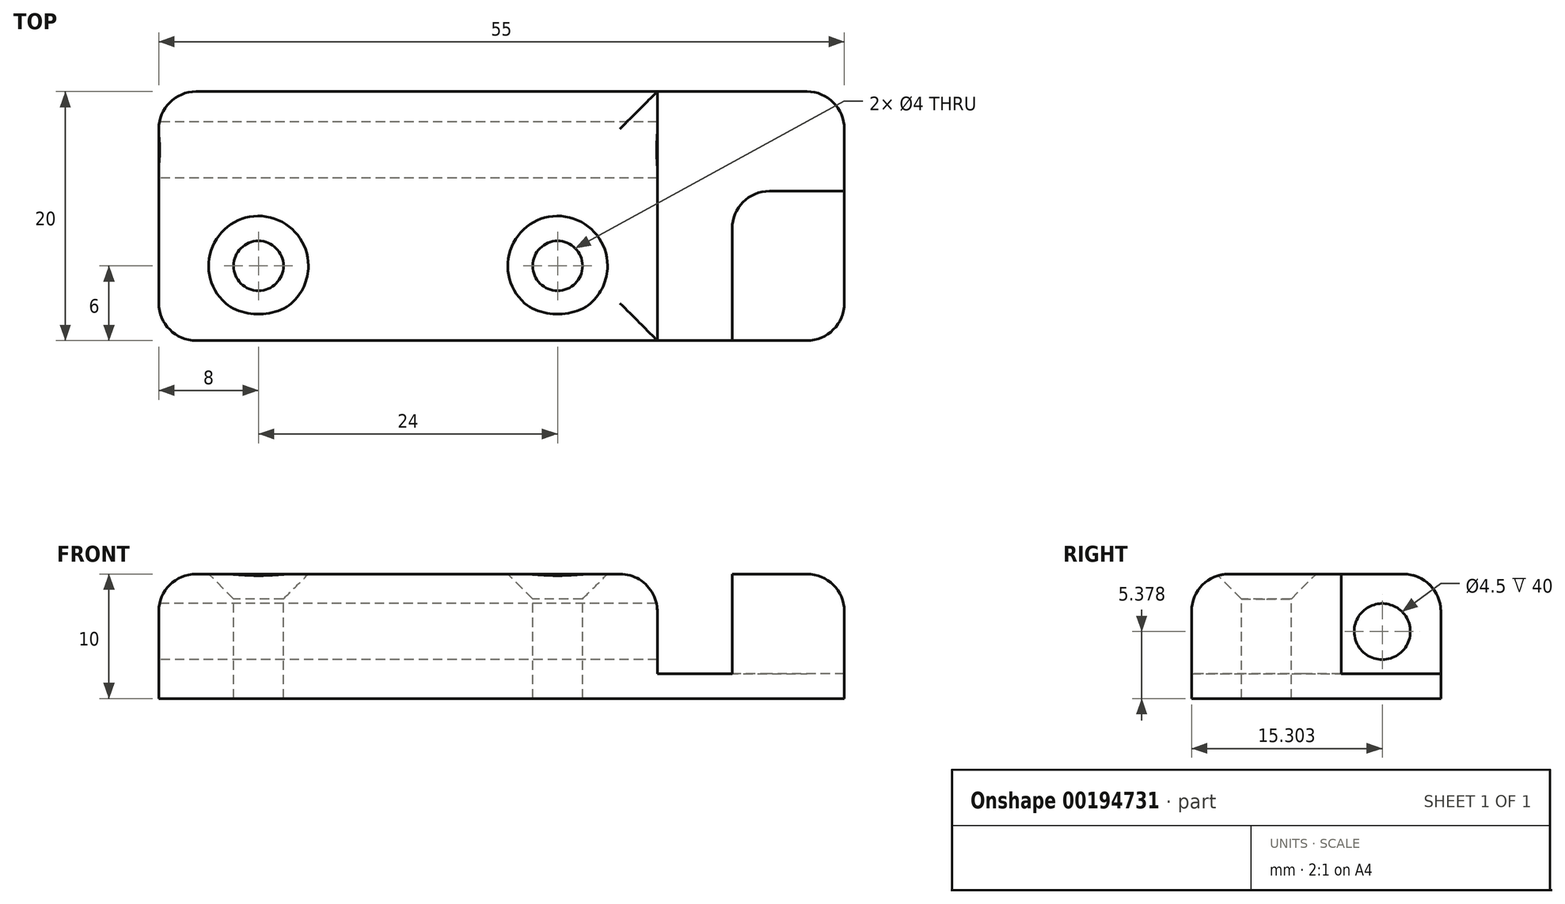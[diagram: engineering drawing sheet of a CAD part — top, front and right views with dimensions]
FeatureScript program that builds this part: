
annotation { "Feature Type Name" : "Feature", "Feature Type Description" : "" }
export const myFeature = defineFeature(function(context is Context, id is Id, definition is map)
    precondition{}
    {
        {
            var Q0;
            Q0=qCreatedBy(makeId("Top.planeOp"),FACE);
            var sketch = newSketch(context, id + "F0", { "sketchPlane" : qUnion([Q0])});
            skLineSegment(sketch, "E0.bottom", {"start": v(0, 0) * mm, "end": v(55, 0) * mm});
            skLineSegment(sketch, "E0.top", {"start": v(0, 20) * mm, "end": v(55, 20) * mm});
            skLineSegment(sketch, "E0.left", {"start": v(0, 0) * mm, "end": v(0, 20) * mm});
            skLineSegment(sketch, "E0.right", {"start": v(55, 0) * mm, "end": v(55, 20) * mm});
            skSolve(sketch);
        }
        {
            var Q0;
            Q0 = qSketchRegion(id + "F0", true);
            extrude(context, id + "F1", {"entities" : qUnion([Q0]), "depth" : 2 * mm});
        }
        {
            var Q0;
            Q0=makeQuery(id+"F1.opExtrude","CAP_FACE",FACE,{"disambiguationData":[OSD([sQuery(id+"F0.wireOp",EDGE,"E0.bottom"),sQuery(id+"F0.wireOp",EDGE,"E0.top"),sQuery(id+"F0.wireOp",EDGE,"E0.left"),sQuery(id+"F0.wireOp",EDGE,"E0.right")])],"isStart":false});
            var sketch = newSketch(context, id + "F2", { "sketchPlane" : qUnion([Q0])});
            skLineSegment(sketch, "E1.bottom", {"start": v(0, 0) * mm, "end": v(40, 0) * mm});
            skLineSegment(sketch, "E1.top", {"start": v(0, 20) * mm, "end": v(40, 20) * mm});
            skLineSegment(sketch, "E1.left", {"start": v(0, 0) * mm, "end": v(0, 20) * mm});
            skLineSegment(sketch, "E1.right", {"start": v(40, 0) * mm, "end": v(40, 20) * mm});
            skPoint(sketch, "E2.endSnap0", {"position": v(55, 10) * mm});
            skLineSegment(sketch, "E3.bottom", {"start": v(55, 12) * mm, "end": v(46, 12) * mm});
            skLineSegment(sketch, "E3.top", {"start": v(55, 0) * mm, "end": v(46, 0) * mm});
            skLineSegment(sketch, "E3.left", {"start": v(55, 12) * mm, "end": v(55, 0) * mm});
            skLineSegment(sketch, "E3.right", {"start": v(46, 12) * mm, "end": v(46, 0) * mm});
            skSolve(sketch);
        }
        {
            var Q0;
            Q0=makeQuery(id+"F2.imprint","IMPRINT",FACE,{"disambiguationData":[TD([[makeQuery(id+"F2.imprint","IMPRINT",EDGE,{"derivedFrom":sQuery(id+"F2.wireOp",EDGE,"E1.bottom")}),1.0]])]});
            var Q1;
            Q1=makeQuery(id+"F2.imprint","IMPRINT",FACE,{"disambiguationData":[TD([[makeQuery(id+"F2.imprint","IMPRINT",EDGE,{"derivedFrom":sQuery(id+"F2.wireOp",EDGE,"E3.bottom")}),1.0]])]});
            extrude(context, id + "F3", {"entities" : qUnion([Q0, Q1]), "operationType" : NewBodyOperationType.ADD, "depth" : 8 * mm});
        }
        {
            var Q0;
            Q0=makeQuery(id+"F3.boolean.opBoolean","MERGE",FACE,{"derivedFrom":[makeQuery(id+"F1.opExtrude","SWEPT_FACE",FACE,{"disambiguationData":[OSD([sQuery(id+"F0.wireOp",EDGE,"E0.left")])]}),makeQuery(id+"F3.opExtrude","SWEPT_FACE",FACE,{"disambiguationData":[OSD([sQuery(id+"F2.wireOp",EDGE,"E1.left")])]})]});
            var sketch = newSketch(context, id + "F4", { "sketchPlane" : qUnion([Q0])});
            skCircle(sketch, "E4", {"center": v(-15.3, 5.38) * mm, "radius": 2.25 * mm});
            skLineSegment(sketch, "E5", {"start": v(-14.14, 5.38) * mm, "end": v(-15.3, 5.38) * mm});
            skSolve(sketch);
        }
        {
            var Q0;
            Q0=makeQuery(id+"F4.imprint","IMPRINT",FACE,{"disambiguationData":[TD([[makeQuery(id+"F4.imprint","IMPRINT",EDGE,{"derivedFrom":sQuery(id+"F4.wireOp",EDGE,"E4")}),1.0]])]});
            extrude(context, id + "F5", {"entities" : qUnion([Q0]), "operationType" : NewBodyOperationType.REMOVE, "oppositeDirection" : true, "depth" : 45 * mm});
        }
        {
            var Q0;
            Q0=makeQuery(id+"F3.opExtrude","CAP_FACE",FACE,{"disambiguationData":[OSD([sQuery(id+"F2.wireOp",EDGE,"E1.bottom"),sQuery(id+"F2.wireOp",EDGE,"E1.top"),sQuery(id+"F2.wireOp",EDGE,"E1.left"),sQuery(id+"F2.wireOp",EDGE,"E1.right")])],"isStart":false});
            var sketch = newSketch(context, id + "F6", { "sketchPlane" : qUnion([Q0])});
            skCircle(sketch, "E6", {"center": v(8, 6) * mm, "radius": 2 * mm});
            skCircle(sketch, "E7", {"center": v(32, 6) * mm, "radius": 2 * mm});
            skCircle(sketch, "E8", {"center": v(8, 6) * mm, "radius": 4 * mm});
            skCircle(sketch, "E9", {"center": v(32, 6) * mm, "radius": 4 * mm});
            skSolve(sketch);
        }
        {
            var Q0;
            Q0=makeQuery(id+"F6.imprint","IMPRINT",FACE,{"disambiguationData":[TD([[makeQuery(id+"F6.imprint","IMPRINT",EDGE,{"derivedFrom":sQuery(id+"F6.wireOp",EDGE,"E6")}),1.0]])]});
            var Q1;
            Q1=makeQuery(id+"F6.imprint","IMPRINT",FACE,{"disambiguationData":[TD([[makeQuery(id+"F6.imprint","IMPRINT",EDGE,{"derivedFrom":sQuery(id+"F6.wireOp",EDGE,"E7")}),1.0]])]});
            extrude(context, id + "F7", {"entities" : qUnion([Q0, Q1]), "operationType" : NewBodyOperationType.REMOVE, "oppositeDirection" : true, "depth" : 25 * mm});
        }
        {
            var Q0;
            Q0=makeQuery(id+"F3.opExtrude","CAP_EDGE",EDGE,{"disambiguationData":[OSD([sQuery(id+"F2.wireOp",EDGE,"E1.top")])],"isStart":false});
            var Q1;
            Q1=makeQuery(id+"F3.opExtrude","CAP_EDGE",EDGE,{"disambiguationData":[OSD([sQuery(id+"F2.wireOp",EDGE,"E1.bottom")])],"isStart":false});
            var Q2;
            Q2=makeQuery(id+"F3.opExtrude","CAP_EDGE",EDGE,{"disambiguationData":[OSD([sQuery(id+"F2.wireOp",EDGE,"E3.top")])],"isStart":false});
            var Q3;
            Q3=makeQuery(id+"F3.opExtrude","CAP_EDGE",EDGE,{"disambiguationData":[OSD([sQuery(id+"F2.wireOp",EDGE,"E1.left")])],"isStart":false});
            var Q4;
            Q4=makeQuery(id+"F3.opExtrude","CAP_EDGE",EDGE,{"disambiguationData":[OSD([sQuery(id+"F2.wireOp",EDGE,"E1.right")])],"isStart":false});
            var Q5;
            Q5=makeQuery(id+"F1.opExtrude","SWEPT_EDGE",EDGE,{"disambiguationData":[OSD([sQuery(id+"F0.wireOp",EDGE,"E0.top"),sQuery(id+"F0.wireOp",EDGE,"E0.right")])]});
            fillet(context, id + "F8", {"entities" : qUnion([Q0, Q1, Q2, Q3, Q4, Q5]), "radius" : 3 * mm, "tangentPropagation" : true, "allowEdgeOverflow" : false});
        }
        {
            var Q0;
            Q0=makeQuery(id+"F3.opExtrude","CAP_FACE",FACE,{"disambiguationData":[OSD([sQuery(id+"F2.wireOp",EDGE,"E1.bottom"),sQuery(id+"F2.wireOp",EDGE,"E1.top"),sQuery(id+"F2.wireOp",EDGE,"E1.left"),sQuery(id+"F2.wireOp",EDGE,"E1.right")])],"isStart":false});
            var sketch = newSketch(context, id + "F9", { "sketchPlane" : qUnion([Q0])});
            skPoint(sketch, "E10", {"position": v(8, 6) * mm});
            skPoint(sketch, "E11", {"position": v(32, 6) * mm});
            skSolve(sketch);
        }
        {
            var Q0;
            Q0=sQuery(id+"F9.wireOp",VERTEX,"E10");
            var Q1;
            Q1=sQuery(id+"F9.wireOp",VERTEX,"E11");
            var Q2;
            Q2=makeQuery(id+"F1.opExtrude","SWEPT_BODY",BODY,{"disambiguationData":[OSD([sQuery(id+"F0.wireOp",EDGE,"E0.bottom"),sQuery(id+"F0.wireOp",EDGE,"E0.top"),sQuery(id+"F0.wireOp",EDGE,"E0.left"),sQuery(id+"F0.wireOp",EDGE,"E0.right")])]});
            hole(context, id + "F10", {"style" : HoleStyle.C_SINK, "endStyle" : HoleEndStyle.BLIND, "holeDiameter" : 4 * mm, "cSinkDiameter" : 8 * mm, "cSinkAngle" : 90 * degree, "holeDepth" : 20 * mm, "isTappedThrough" : true, "tappedDepth" : 12 * mm, "tapClearance" : 3, "startFromSketch" : true, "locations" : qUnion([Q0, Q1]), "scope" : qUnion([Q2])});
        }
        {
            var Q0;
            Q0=makeQuery(id+"F3.boolean.opBoolean","MERGE",EDGE,{"derivedFrom":[makeQuery(id+"F1.opExtrude","SWEPT_EDGE",EDGE,{"disambiguationData":[OSD([sQuery(id+"F0.wireOp",EDGE,"E0.bottom"),sQuery(id+"F0.wireOp",EDGE,"E0.left")])]}),makeQuery(id+"F3.opExtrude","SWEPT_EDGE",EDGE,{"disambiguationData":[OSD([sQuery(id+"F2.wireOp",EDGE,"E1.bottom"),sQuery(id+"F2.wireOp",EDGE,"E1.left")])]})]});
            var Q1;
            Q1=makeQuery(id+"F3.boolean.opBoolean","MERGE",EDGE,{"derivedFrom":[makeQuery(id+"F1.opExtrude","SWEPT_EDGE",EDGE,{"disambiguationData":[OSD([sQuery(id+"F0.wireOp",EDGE,"E0.top"),sQuery(id+"F0.wireOp",EDGE,"E0.left")])]}),makeQuery(id+"F3.opExtrude","SWEPT_EDGE",EDGE,{"disambiguationData":[OSD([sQuery(id+"F2.wireOp",EDGE,"E1.top"),sQuery(id+"F2.wireOp",EDGE,"E1.left")])]})]});
            var Q2;
            Q2=makeQuery(id+"F3.boolean.opBoolean","MERGE",EDGE,{"derivedFrom":[makeQuery(id+"F1.opExtrude","SWEPT_EDGE",EDGE,{"disambiguationData":[OSD([sQuery(id+"F0.wireOp",EDGE,"E0.bottom"),sQuery(id+"F0.wireOp",EDGE,"E0.right")])]}),makeQuery(id+"F3.opExtrude","SWEPT_EDGE",EDGE,{"disambiguationData":[OSD([sQuery(id+"F2.wireOp",EDGE,"E3.top"),sQuery(id+"F2.wireOp",EDGE,"E3.left")])]})]});
            fillet(context, id + "F11", {"entities" : qUnion([Q0, Q1, Q2]), "radius" : 3 * mm, "tangentPropagation" : true, "allowEdgeOverflow" : false});
        }
        {
            var Q0;
            Q0=makeQuery(id+"F3.opExtrude","SWEPT_EDGE",EDGE,{"disambiguationData":[OSD([sQuery(id+"F2.wireOp",EDGE,"E3.bottom"),sQuery(id+"F2.wireOp",EDGE,"E3.right")])]});
            fillet(context, id + "F12", {"entities" : qUnion([Q0]), "radius" : 3 * mm, "tangentPropagation" : true, "allowEdgeOverflow" : false});
        }
    });
